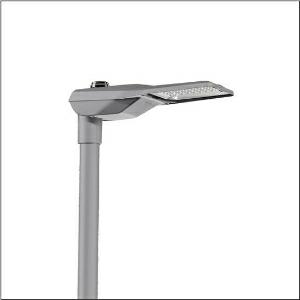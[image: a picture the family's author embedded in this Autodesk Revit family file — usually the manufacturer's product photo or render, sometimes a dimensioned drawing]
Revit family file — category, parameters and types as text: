
# Revit family: streetlight_sl_21_mini___p0_8a_5xe6u27n08gb_261a
name_source: partatom
category: Lighting Fixtures
units: mm (PartAtom-declared; Revit-internal decimal feet)

## family parameters
Cut with Voids When Loaded = No
Host = Face
Light Source = No
Part Type = Normal
Room Calculation Point = No
Round Connector Dimension = Use Diameter
Shared = No

## types (1)
- --- (1 x LED, 4960 lm, 40.4 W, 2200K)
    Apparent Load = 40 VA
    CIE Flux Codes = 33 69 96 100 100
    Color Rendering = 70
    Color Temperature = 2200K
    Default Elevation = 1800 mm
    Description = Streetlight SL 21 mini, mast luminaire, primary light control with lens, of PMMA, primary optical cover: cover, of toughened safety glass, transparent, light distribution: P0.8a, light emission: direct distribution, primary light characteristic: asymmetric, installation type: side-entry, LED, 3G 1.5mm², High Power LED, rated luminous flux: 4.960lm, luminous efficacy: 123lm/W, light colour: 722, colour temperature: 2200K, control gear: NEMA (7pin), control: flexible luminous flux parameterisation, time-dependent luminous flux control, constant luminous flux control, pre-setting: linear dimming characteristic, overheat protection, mains connection: 230..240V, AC, 50/60Hz, connection cable pre-assembled, cable length: 8,5m, wiring characteristics: H07RN-F, start of lifetime: 40W, end of service life: 41W, reduction: 19W, luminaire housing, of diecast aluminium (EN AC-44300), powder-coated, Siteco® metallic grey (DB 702S), corrosivity category C5 mid according to DIN EN ISO 12944, multi-level sealing system, sealing non-destructively replaceable, inclination adjustable: 0°, 5°, 10°, 15°, length: 628mm, width: 235mm, height: 110mm, spigot size: 42mm (side-entry), mounting height: 4..8m, protection rating (complete): IP66, insulation class (complete): insulation class I (protective earthing), certification: CE, ENEC, ENEC+, VDE, impact resistance: IK10, permissible operating ambient temperature for outdoor applications: -40..+50°C, standard-compliant lighting for roads and squares, packaging unit: 1 piece

Light Distribution: P0.8a
    Height = 110 mm
    Lamp = 1 x LED
    Lamp Light Flux = 4960 lm
    Lamp Power = 40.4 W
    Lamp count = 1
    Length = 625 mm
    Luminous efficacy = 123 lm/W
    Manufacturer = Siteco
    ModVariant = No
    Model = 5XE6U27N08GB
    Number of Poles = 1
    OnlyDefault = Yes
    Power Factor = 1
    Product Name = Streetlight SL 21 mini | P0.8a
    Product group = mast luminaire | pylon top
    ProductGroupID = 6100
    Protection Class = Protection class I
    Protection Degree = IP 66
    RLX_Detail_Level = 1
    RLX_Emergency_Light_Flux = 0 lm
    RLX_Emergency_Type = 0
    RLX_Emergency_Type_DB = No
    RlxData = <blob elided: 25593 chars, md5=d606e45f>
    Socket = socket
    Standby Power = 0 W
    System Light Flux = 4960 lm
    System Power = 40 W
    Type Comments = factory setting: luminous flux: 100 % | dim-lin: 254 | 812 mA
    Type Image = l_1294379.jpg
    URL = http://relux.com
    VarID = @adj_073622
    Voltage = 0 V
    Weight = 0.00 kg
    Width = 234 mm

## geometry (parser evidence)
native form markers: Blend x4, Sweep x11
no freeform markers — native parametric forms only
